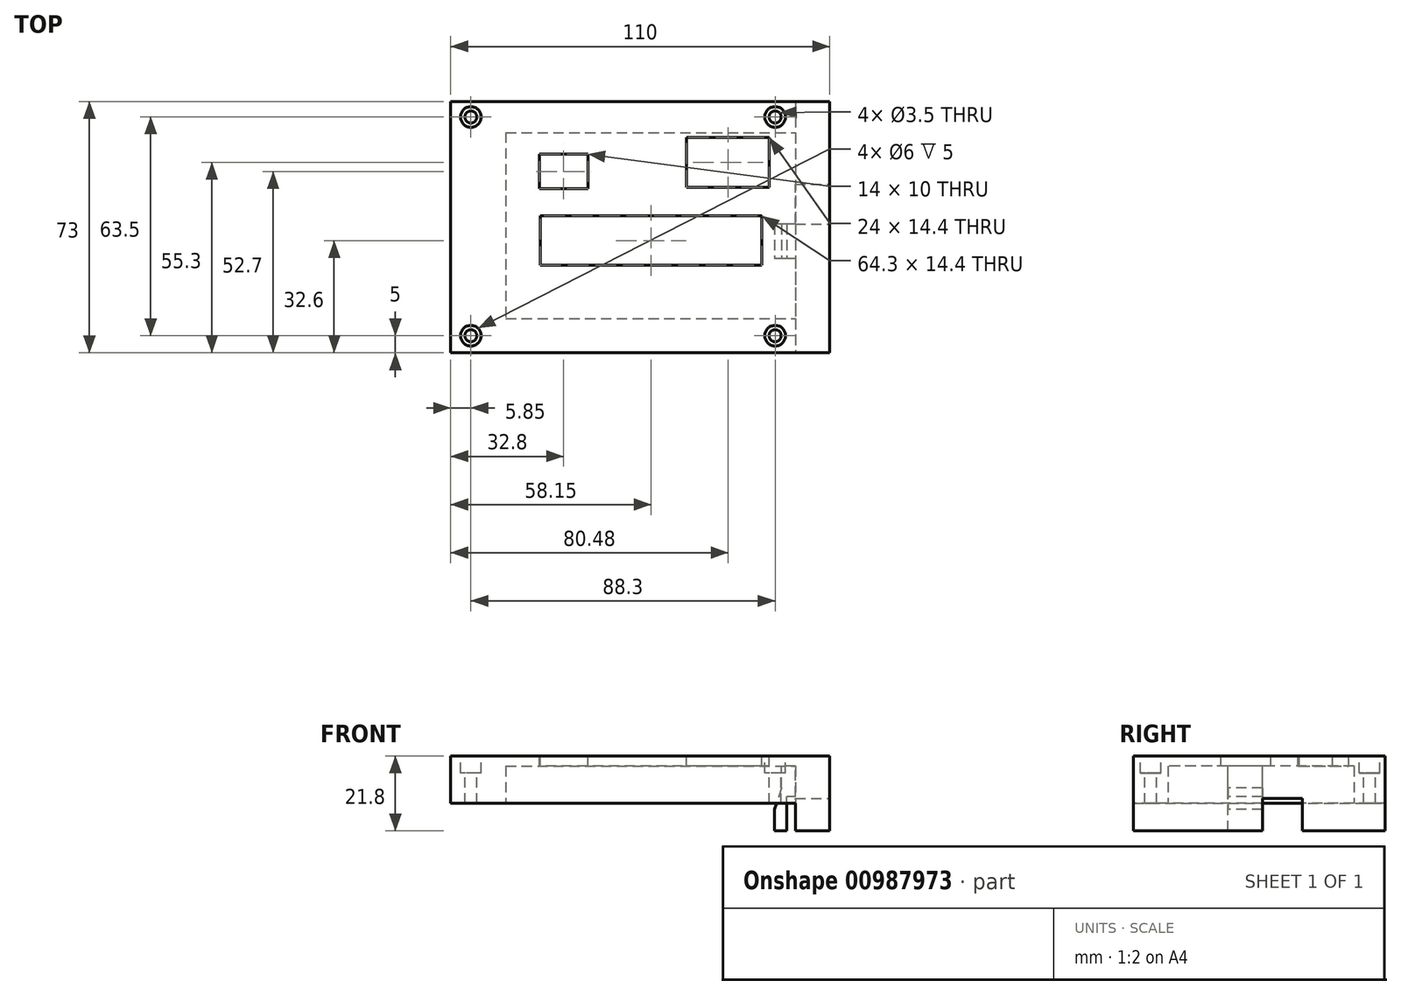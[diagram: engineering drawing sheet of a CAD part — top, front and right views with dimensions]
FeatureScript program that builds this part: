
annotation { "Feature Type Name" : "Feature", "Feature Type Description" : "" }
export const myFeature = defineFeature(function(context is Context, id is Id, definition is map)
    precondition{}
    {
        {
            var Q0;
            Q0=qCreatedBy(makeId("Top.planeOp"),FACE);
            var sketch = newSketch(context, id + "F0", { "sketchPlane" : qUnion([Q0])});
            skLineSegment(sketch, "E0.bottom", {"start": v(0, 0) * mm, "end": v(110, 0) * mm});
            skLineSegment(sketch, "E0.top", {"start": v(0, 73) * mm, "end": v(110, 73) * mm});
            skLineSegment(sketch, "E0.left", {"start": v(0, 0) * mm, "end": v(0, 73) * mm});
            skLineSegment(sketch, "E0.right", {"start": v(110, 0) * mm, "end": v(110, 73) * mm});
            skSolve(sketch);
        }
        {
            var Q0;
            Q0 = qSketchRegion(id + "F0", true);
            extrude(context, id + "F1", {"entities" : qUnion([Q0]), "depth" : 13.8 * mm, "offsetDistance" : 25 * mm});
        }
        {
            var Q0;
            Q0=makeQuery(id+"F1.opExtrude","CAP_FACE",FACE,{"disambiguationData":[OSD([sQuery(id+"F0.wireOp",EDGE,"E0.bottom"),sQuery(id+"F0.wireOp",EDGE,"E0.top"),sQuery(id+"F0.wireOp",EDGE,"E0.left"),sQuery(id+"F0.wireOp",EDGE,"E0.right")])],"isStart":true});
            var sketch = newSketch(context, id + "F2", { "sketchPlane" : qUnion([Q0])});
            skLineSegment(sketch, "E1.bottom", {"start": v(16, -64) * mm, "end": v(100, -64) * mm});
            skLineSegment(sketch, "E1.top", {"start": v(16, -10) * mm, "end": v(100, -10) * mm});
            skLineSegment(sketch, "E1.left", {"start": v(16, -64) * mm, "end": v(16, -10) * mm});
            skLineSegment(sketch, "E1.right", {"start": v(100, -64) * mm, "end": v(100, -10) * mm});
            skSolve(sketch);
        }
        {
            var Q0;
            Q0 = qSketchRegion(id + "F2", true);
            extrude(context, id + "F3", {"entities" : qUnion([Q0]), "operationType" : NewBodyOperationType.REMOVE, "oppositeDirection" : true, "depth" : 10.8 * mm, "offsetDistance" : 25 * mm});
        }
        {
            var Q0;
            Q0=makeQuery(id+"F1.opExtrude","CAP_FACE",FACE,{"disambiguationData":[OSD([sQuery(id+"F0.wireOp",EDGE,"E0.bottom"),sQuery(id+"F0.wireOp",EDGE,"E0.top"),sQuery(id+"F0.wireOp",EDGE,"E0.left"),sQuery(id+"F0.wireOp",EDGE,"E0.right")])],"isStart":true});
            var sketch = newSketch(context, id + "F4", { "sketchPlane" : qUnion([Q0])});
            skLineSegment(sketch, "E2.bottom", {"start": v(110, -73) * mm, "end": v(100, -73) * mm});
            skLineSegment(sketch, "E2.top", {"start": v(110, 0) * mm, "end": v(100, 0) * mm});
            skLineSegment(sketch, "E2.left", {"start": v(110, -73) * mm, "end": v(110, 0) * mm});
            skLineSegment(sketch, "E2.right", {"start": v(100, -73) * mm, "end": v(100, 0) * mm});
            skSolve(sketch);
        }
        {
            var Q0;
            Q0 = qSketchRegion(id + "F4", true);
            extrude(context, id + "F5", {"entities" : qUnion([Q0]), "operationType" : NewBodyOperationType.ADD, "depth" : 8 * mm, "offsetDistance" : 25 * mm});
        }
        {
            var Q0;
            Q0=makeQuery(id+"F1.opExtrude","CAP_FACE",FACE,{"disambiguationData":[OSD([sQuery(id+"F0.wireOp",EDGE,"E0.bottom"),sQuery(id+"F0.wireOp",EDGE,"E0.top"),sQuery(id+"F0.wireOp",EDGE,"E0.left"),sQuery(id+"F0.wireOp",EDGE,"E0.right")])],"isStart":false});
            var sketch = newSketch(context, id + "F6", { "sketchPlane" : qUnion([Q0])});
            skCircle(sketch, "E3", {"center": v(5.85, 5) * mm, "radius": 1.75 * mm});
            skCircle(sketch, "E4", {"center": v(94.15, 5) * mm, "radius": 1.75 * mm});
            skCircle(sketch, "E5", {"center": v(94.15, 68.5) * mm, "radius": 1.75 * mm});
            skCircle(sketch, "E6", {"center": v(5.85, 68.5) * mm, "radius": 1.75 * mm});
            skSolve(sketch);
        }
        {
            var Q0;
            Q0 = qSketchRegion(id + "F6", true);
            extrude(context, id + "F7", {"entities" : qUnion([Q0]), "operationType" : NewBodyOperationType.REMOVE, "oppositeDirection" : true, "depth" : 25 * mm, "offsetDistance" : 25 * mm});
        }
        {
            var Q0;
            Q0=makeQuery(id+"F1.opExtrude","CAP_FACE",FACE,{"disambiguationData":[OSD([sQuery(id+"F0.wireOp",EDGE,"E0.bottom"),sQuery(id+"F0.wireOp",EDGE,"E0.top"),sQuery(id+"F0.wireOp",EDGE,"E0.left"),sQuery(id+"F0.wireOp",EDGE,"E0.right")])],"isStart":false});
            var sketch = newSketch(context, id + "F8", { "sketchPlane" : qUnion([Q0])});
            skCircle(sketch, "E7", {"center": v(5.85, 68.5) * mm, "radius": 3 * mm});
            skCircle(sketch, "E8", {"center": v(5.85, 5) * mm, "radius": 3 * mm});
            skCircle(sketch, "E9", {"center": v(94.15, 5) * mm, "radius": 3 * mm});
            skCircle(sketch, "E10", {"center": v(94.15, 68.5) * mm, "radius": 3 * mm});
            skSolve(sketch);
        }
        {
            var Q0;
            Q0 = qSketchRegion(id + "F8", true);
            extrude(context, id + "F9", {"entities" : qUnion([Q0]), "operationType" : NewBodyOperationType.REMOVE, "oppositeDirection" : true, "depth" : 5 * mm, "offsetDistance" : 25 * mm});
        }
        {
            var Q0;
            Q0=makeQuery(id+"F1.opExtrude","CAP_FACE",FACE,{"disambiguationData":[OSD([sQuery(id+"F0.wireOp",EDGE,"E0.bottom"),sQuery(id+"F0.wireOp",EDGE,"E0.top"),sQuery(id+"F0.wireOp",EDGE,"E0.left"),sQuery(id+"F0.wireOp",EDGE,"E0.right")])],"isStart":false});
            var sketch = newSketch(context, id + "F10", { "sketchPlane" : qUnion([Q0])});
            skLineSegment(sketch, "E11.bottom", {"start": v(26, 25.4) * mm, "end": v(90.3, 25.4) * mm});
            skLineSegment(sketch, "E11.top", {"start": v(26, 39.8) * mm, "end": v(90.3, 39.8) * mm});
            skLineSegment(sketch, "E11.left", {"start": v(26, 25.4) * mm, "end": v(26, 39.8) * mm});
            skLineSegment(sketch, "E11.right", {"start": v(90.3, 25.4) * mm, "end": v(90.3, 39.8) * mm});
            skLineSegment(sketch, "E12.bottom", {"start": v(68.48, 62.5) * mm, "end": v(92.48, 62.5) * mm});
            skLineSegment(sketch, "E12.top", {"start": v(68.48, 48.1) * mm, "end": v(92.48, 48.1) * mm});
            skLineSegment(sketch, "E12.left", {"start": v(68.48, 62.5) * mm, "end": v(68.48, 48.1) * mm});
            skLineSegment(sketch, "E12.right", {"start": v(92.48, 62.5) * mm, "end": v(92.48, 48.1) * mm});
            skLineSegment(sketch, "E13.bottom", {"start": v(25.8, 57.7) * mm, "end": v(39.8, 57.7) * mm});
            skLineSegment(sketch, "E13.top", {"start": v(25.8, 47.7) * mm, "end": v(39.8, 47.7) * mm});
            skLineSegment(sketch, "E13.left", {"start": v(25.8, 57.7) * mm, "end": v(25.8, 47.7) * mm});
            skLineSegment(sketch, "E13.right", {"start": v(39.8, 57.7) * mm, "end": v(39.8, 47.7) * mm});
            skSolve(sketch);
        }
        {
            var Q0;
            Q0 = qSketchRegion(id + "F10", true);
            extrude(context, id + "F11", {"entities" : qUnion([Q0]), "operationType" : NewBodyOperationType.REMOVE, "oppositeDirection" : true, "depth" : 25 * mm, "offsetDistance" : 25 * mm});
        }
        {
            var Q0;
            Q0=makeQuery(id+"F5.boolean.opBoolean","MERGE",FACE,{"derivedFrom":[makeQuery(id+"F1.opExtrude","SWEPT_FACE",FACE,{"disambiguationData":[OSD([sQuery(id+"F0.wireOp",EDGE,"E0.right")])]}),makeQuery(id+"F5.opExtrude","SWEPT_FACE",FACE,{"disambiguationData":[OSD([sQuery(id+"F4.wireOp",EDGE,"E2.left")])]})]});
            var sketch = newSketch(context, id + "F12", { "sketchPlane" : qUnion([Q0])});
            skLineSegment(sketch, "E14.bottom", {"start": v(37.4, -8) * mm, "end": v(49, -8) * mm});
            skLineSegment(sketch, "E14.top", {"start": v(37.4, 1.5) * mm, "end": v(49, 1.5) * mm});
            skLineSegment(sketch, "E14.left", {"start": v(37.4, -8) * mm, "end": v(37.4, 1.5) * mm});
            skLineSegment(sketch, "E14.right", {"start": v(49, -8) * mm, "end": v(49, 1.5) * mm});
            skSolve(sketch);
        }
        {
            var Q0;
            Q0 = qSketchRegion(id + "F12", true);
            extrude(context, id + "F13", {"entities" : qUnion([Q0]), "operationType" : NewBodyOperationType.REMOVE, "oppositeDirection" : true, "depth" : 25 * mm, "offsetDistance" : 25 * mm});
        }
        {
            var Q0;
            Q0=makeQuery(id+"F5.boolean.opBoolean","MERGE",FACE,{"derivedFrom":[makeQuery(id+"F1.opExtrude","SWEPT_FACE",FACE,{"disambiguationData":[OSD([sQuery(id+"F0.wireOp",EDGE,"E0.bottom")])]}),makeQuery(id+"F5.opExtrude","SWEPT_FACE",FACE,{"disambiguationData":[OSD([sQuery(id+"F4.wireOp",EDGE,"E2.top")])]})]});
            var sketch = newSketch(context, id + "F14", { "sketchPlane" : qUnion([Q0])});
            skLineSegment(sketch, "E15.bottom", {"start": v(97.5, -8) * mm, "end": v(94, -8) * mm});
            skLineSegment(sketch, "E15.left", {"start": v(100, 2) * mm, "end": v(100, 4.5) * mm});
            skLineSegment(sketch, "E15.right", {"start": v(94, -8) * mm, "end": v(94, -1.75) * mm});
            skLineSegment(sketch, "E16.top", {"start": v(100, 13.8) * mm, "end": v(96, 13.8) * mm});
            skLineSegment(sketch, "E16.left", {"start": v(100, 4.5) * mm, "end": v(100, 13.8) * mm});
            skLineSegment(sketch, "E16.right", {"start": v(96, 4.5) * mm, "end": v(96, 13.8) * mm});
            skLineSegment(sketch, "E17", {"start": v(96, 4.5) * mm, "end": v(94, -1.75) * mm});
            skPoint(sketch, "E18.orphan", {"position": v(94, 4.5) * mm});
            skLineSegment(sketch, "E19.top", {"start": v(100, 2) * mm, "end": v(97.5, 2) * mm});
            skLineSegment(sketch, "E19.right", {"start": v(97.5, -8) * mm, "end": v(97.5, 2) * mm});
            skSolve(sketch);
        }
        {
            var Q0;
            Q0 = qSketchRegion(id + "F14", true);
            extrude(context, id + "F15", {"entities" : qUnion([Q0]), "operationType" : NewBodyOperationType.ADD, "oppositeDirection" : true, "depth" : 37.4 * mm, "offsetDistance" : 25 * mm, "hasSecondDirection" : true, "secondDirectionOppositeDirection" : true, "secondDirectionDepth" : 27.4 * mm});
        }
        {
            var Q0;
            Q0=makeQuery(id+"F5.boolean.opBoolean","MERGE",FACE,{"derivedFrom":[makeQuery(id+"F1.opExtrude","SWEPT_FACE",FACE,{"disambiguationData":[OSD([sQuery(id+"F0.wireOp",EDGE,"E0.top")])]}),makeQuery(id+"F5.opExtrude","SWEPT_FACE",FACE,{"disambiguationData":[OSD([sQuery(id+"F4.wireOp",EDGE,"E2.bottom")])]})]});
            cPlane(context, id + "F16", {"entities" : qUnion([Q0]), "cplaneType" : CPlaneType.OFFSET, "offset" : 29.8 * mm, "oppositeDirection" : true, "width" : 150 * mm, "height" : 150 * mm});
        }
    });
